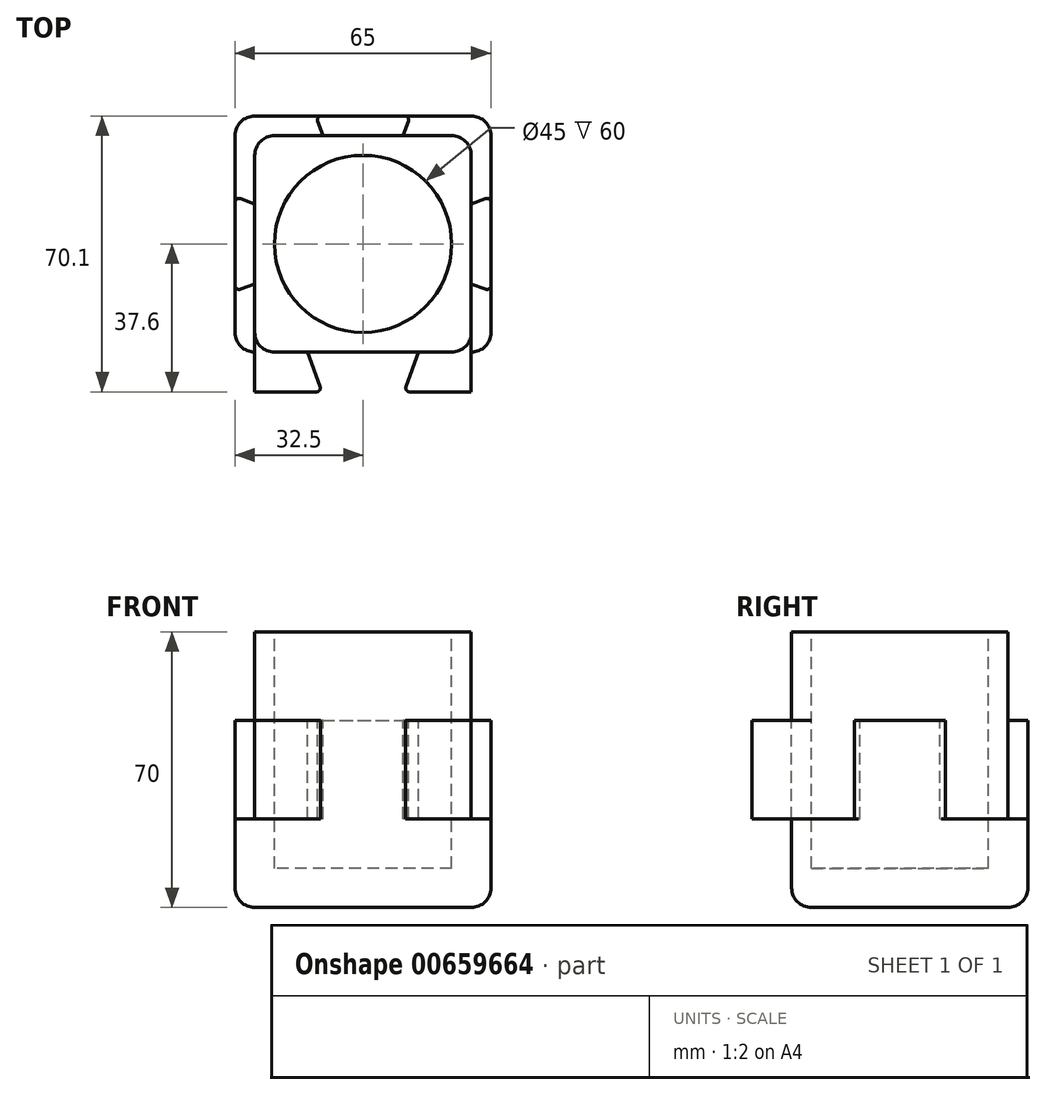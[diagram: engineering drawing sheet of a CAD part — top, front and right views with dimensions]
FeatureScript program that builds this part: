
annotation { "Feature Type Name" : "Feature", "Feature Type Description" : "" }
export const myFeature = defineFeature(function(context is Context, id is Id, definition is map)
    precondition{}
    {
        {
            var Q0;
            Q0=qCreatedBy(makeId("Top.planeOp"),FACE);
            var sketch = newSketch(context, id + "F0", { "sketchPlane" : qUnion([Q0])});
            skLineSegment(sketch, "E0.bottom", {"start": v(-27.5, 27.5) * mm, "end": v(27.5, 27.5) * mm});
            skLineSegment(sketch, "E0.top", {"start": v(-27.5, -27.5) * mm, "end": v(27.5, -27.5) * mm});
            skLineSegment(sketch, "E0.left", {"start": v(-27.5, 27.5) * mm, "end": v(-27.5, -27.5) * mm});
            skLineSegment(sketch, "E0.right", {"start": v(27.5, 27.5) * mm, "end": v(27.5, -27.5) * mm});
            skPoint(sketch, "E0.middle", {"position": v(0, 0) * mm});
            skLineSegment(sketch, "E1", {"start": v(27.5, -10.18) * mm, "end": v(32.5, -12) * mm});
            skLineSegment(sketch, "E2", {"start": v(32.5, -12) * mm, "end": v(32.5, 12) * mm});
            skLineSegment(sketch, "E3", {"start": v(32.5, 12) * mm, "end": v(27.5, 10.18) * mm});
            skPoint(sketch, "E4", {"position": v(32.5, 0) * mm});
            skLineSegment(sketch, "E5", {"start": v(-10.18, 27.5) * mm, "end": v(-12, 32.5) * mm});
            skLineSegment(sketch, "E6", {"start": v(-12, 32.5) * mm, "end": v(12, 32.5) * mm});
            skLineSegment(sketch, "E7", {"start": v(12, 32.5) * mm, "end": v(10.18, 27.5) * mm});
            skPoint(sketch, "E8", {"position": v(0, 32.5) * mm});
            skLineSegment(sketch, "E9", {"start": v(-27.5, 10.18) * mm, "end": v(-32.5, 12) * mm});
            skLineSegment(sketch, "E10", {"start": v(-32.5, 12) * mm, "end": v(-32.5, -12) * mm});
            skLineSegment(sketch, "E11", {"start": v(-32.5, -12) * mm, "end": v(-27.5, -10.18) * mm});
            skPoint(sketch, "E12", {"position": v(-32.5, 0) * mm});
            skLineSegment(sketch, "E13", {"start": v(-27.5, -27.5) * mm, "end": v(-27.5, -37.6) * mm});
            skLineSegment(sketch, "E14", {"start": v(-27.5, -37.6) * mm, "end": v(-10.42, -37.6) * mm});
            skLineSegment(sketch, "E15", {"start": v(-10.42, -37.6) * mm, "end": v(-14.1, -27.5) * mm});
            skLineSegment(sketch, "E16", {"start": v(27.5, -27.5) * mm, "end": v(27.5, -37.6) * mm});
            skLineSegment(sketch, "E17", {"start": v(27.5, -37.6) * mm, "end": v(10.42, -37.6) * mm});
            skLineSegment(sketch, "E18", {"start": v(10.42, -37.6) * mm, "end": v(14.1, -27.5) * mm});
            skSolve(sketch);
        }
        {
            var Q0;
            {var subQ1=sQuery(id+"F0.wireOp",EDGE,"E0.bottom");Q0=makeQuery(id+"F0.imprint","IMPRINT",FACE,{"disambiguationData":[TD([[makeQuery(id+"F0.imprint","IMPRINT",EDGE,{"derivedFrom":subQ1}),-1.0]])]});}
            extrude(context, id + "F1", {"entities" : qUnion([Q0]), "oppositeDirection" : true, "depth" : 70 * mm, "offsetDistance" : 25 * mm, "symmetric" : true});
        }
        {
            var Q0;
            {var subQ0=sQuery(id+"F0.wireOp",EDGE,"E5");Q0=makeQuery(id+"F0.imprint","IMPRINT",FACE,{"disambiguationData":[TD([[makeQuery(id+"F0.imprint","IMPRINT",EDGE,{"derivedFrom":subQ0}),-1.0]])]});}
            var Q1;
            {var subQ0=sQuery(id+"F0.wireOp",EDGE,"E9");Q1=makeQuery(id+"F0.imprint","IMPRINT",FACE,{"disambiguationData":[TD([[makeQuery(id+"F0.imprint","IMPRINT",EDGE,{"derivedFrom":subQ0}),1.0]])]});}
            var Q2;
            {var subQ2=sQuery(id+"F0.wireOp",EDGE,"E13");Q2=makeQuery(id+"F0.imprint","IMPRINT",FACE,{"disambiguationData":[TD([[makeQuery(id+"F0.imprint","IMPRINT",EDGE,{"derivedFrom":subQ2}),1.0]])]});}
            var Q3;
            {var subQ0=sQuery(id+"F0.wireOp",EDGE,"E16");Q3=makeQuery(id+"F0.imprint","IMPRINT",FACE,{"disambiguationData":[TD([[makeQuery(id+"F0.imprint","IMPRINT",EDGE,{"derivedFrom":subQ0}),-1.0]])]});}
            var Q4;
            {var subQ2=sQuery(id+"F0.wireOp",EDGE,"E1");Q4=makeQuery(id+"F0.imprint","IMPRINT",FACE,{"disambiguationData":[TD([[makeQuery(id+"F0.imprint","IMPRINT",EDGE,{"derivedFrom":subQ2}),1.0]])]});}
            extrude(context, id + "F2", {"entities" : qUnion([Q0, Q1, Q2, Q3, Q4]), "operationType" : NewBodyOperationType.ADD, "oppositeDirection" : true, "depth" : 25 * mm, "offsetDistance" : 25 * mm, "symmetric" : true});
        }
        {
            var Q0;
            Q0=makeQuery(id+"F1.opExtrude","CAP_FACE",FACE,{"disambiguationData":[OSD([sQuery(id+"F0.wireOp",EDGE,"E0.bottom"),sQuery(id+"F0.wireOp",EDGE,"E0.top"),sQuery(id+"F0.wireOp",EDGE,"E0.left"),sQuery(id+"F0.wireOp",EDGE,"E0.right")])],"isStart":false});
            var sketch = newSketch(context, id + "F3", { "sketchPlane" : qUnion([Q0])});
            skLineSegment(sketch, "E19", {"start": v(27.5, -27.5) * mm, "end": v(27.5, 27.5) * mm});
            skLineSegment(sketch, "E20", {"start": v(27.5, 27.5) * mm, "end": v(-27.5, 27.5) * mm});
            skLineSegment(sketch, "E21", {"start": v(27.5, -27.5) * mm, "end": v(-27.5, -27.5) * mm});
            skLineSegment(sketch, "E22", {"start": v(-27.5, -27.5) * mm, "end": v(-27.5, 27.5) * mm});
            skLineSegment(sketch, "E23", {"start": v(-32.5, 27.5) * mm, "end": v(32.5, 27.5) * mm});
            skLineSegment(sketch, "E24", {"start": v(32.5, 27.5) * mm, "end": v(32.5, -32.5) * mm});
            skLineSegment(sketch, "E25", {"start": v(32.5, -32.5) * mm, "end": v(-32.5, -32.5) * mm});
            skLineSegment(sketch, "E26", {"start": v(-32.5, -32.5) * mm, "end": v(-32.5, 27.5) * mm});
            skSolve(sketch);
        }
        {
            var Q0;
            Q0 = qSketchRegion(id + "F3", true);
            var Q1;
            Q1=makeQuery(id+"F2.opExtrude","CAP_FACE",FACE,{"disambiguationData":[OSD([sQuery(id+"F0.wireOp",EDGE,"E0.left"),sQuery(id+"F0.wireOp",EDGE,"E9"),sQuery(id+"F0.wireOp",EDGE,"E10"),sQuery(id+"F0.wireOp",EDGE,"E11")])],"isStart":false});
            extrude(context, id + "F4", {"entities" : qUnion([Q0]), "operationType" : NewBodyOperationType.ADD, "endBound" : BoundingType.UP_TO_SURFACE, "oppositeDirection" : true, "depth" : 25 * mm, "endBoundEntityFace" : qUnion([Q1]), "offsetDistance" : 25 * mm});
        }
        {
            var Q0;
            Q0=makeQuery(id+"F1.opExtrude","CAP_FACE",FACE,{"disambiguationData":[OSD([sQuery(id+"F0.wireOp",EDGE,"E0.bottom"),sQuery(id+"F0.wireOp",EDGE,"E0.top"),sQuery(id+"F0.wireOp",EDGE,"E0.left"),sQuery(id+"F0.wireOp",EDGE,"E0.right")])],"isStart":true});
            var sketch = newSketch(context, id + "F5", { "sketchPlane" : qUnion([Q0])});
            skCircle(sketch, "E27", {"center": v(0, 0) * mm, "radius": 22.5 * mm});
            skSolve(sketch);
        }
        {
            var Q0;
            Q0 = qSketchRegion(id + "F5", true);
            extrude(context, id + "F6", {"entities" : qUnion([Q0]), "operationType" : NewBodyOperationType.REMOVE, "oppositeDirection" : true, "depth" : 60 * mm, "offsetDistance" : 25 * mm});
        }
        {
            var Q0;
            {var subQ0=sQuery(id+"F0.wireOp",EDGE,"E13");var subQ1=sQuery(id+"F0.wireOp",EDGE,"E0.top");var subQ2=sQuery(id+"F0.wireOp",EDGE,"E0.left");Q0=makeQuery(id+"F2.boolean.opBoolean","SPLIT",EDGE,{"disambiguationData":[TD([makeQuery(id+"F1.opExtrude","CAP_FACE",FACE,{"disambiguationData":[OSD([sQuery(id+"F0.wireOp",EDGE,"E0.bottom"),subQ1,subQ2,sQuery(id+"F0.wireOp",EDGE,"E0.right")])],"isStart":true})])],"derivedFrom":makeQuery(id+"F1.opExtrude","SWEPT_EDGE",EDGE,{"disambiguationData":[OSD([subQ1,subQ2,subQ0])]})});}
            var Q1;
            Q1=makeQuery(id+"F4.opExtrude","SWEPT_EDGE",EDGE,{"disambiguationData":[OSD([sQuery(id+"F3.wireOp",EDGE,"E23"),sQuery(id+"F3.wireOp",EDGE,"E26")])]});
            var Q2;
            {var subQ0=sQuery(id+"F0.wireOp",EDGE,"E0.right");var subQ1=sQuery(id+"F0.wireOp",EDGE,"E16");var subQ2=sQuery(id+"F0.wireOp",EDGE,"E0.top");Q2=makeQuery(id+"F2.boolean.opBoolean","SPLIT",EDGE,{"disambiguationData":[TD([makeQuery(id+"F1.opExtrude","CAP_FACE",FACE,{"disambiguationData":[OSD([sQuery(id+"F0.wireOp",EDGE,"E0.bottom"),subQ2,sQuery(id+"F0.wireOp",EDGE,"E0.left"),subQ0])],"isStart":true})])],"derivedFrom":makeQuery(id+"F1.opExtrude","SWEPT_EDGE",EDGE,{"disambiguationData":[OSD([subQ2,subQ0,subQ1])]})});}
            var Q3;
            Q3=makeQuery(id+"F4.opExtrude","SWEPT_EDGE",EDGE,{"disambiguationData":[OSD([sQuery(id+"F3.wireOp",EDGE,"E23"),sQuery(id+"F3.wireOp",EDGE,"E24")])]});
            var Q4;
            Q4=makeQuery(id+"F1.opExtrude","SWEPT_EDGE",EDGE,{"disambiguationData":[OSD([sQuery(id+"F0.wireOp",EDGE,"E0.bottom"),sQuery(id+"F0.wireOp",EDGE,"E0.right")])]});
            var Q5;
            Q5=makeQuery(id+"F4.opExtrude","SWEPT_EDGE",EDGE,{"disambiguationData":[OSD([sQuery(id+"F3.wireOp",EDGE,"E24"),sQuery(id+"F3.wireOp",EDGE,"E25")])]});
            var Q6;
            Q6=makeQuery(id+"F1.opExtrude","SWEPT_EDGE",EDGE,{"disambiguationData":[OSD([sQuery(id+"F0.wireOp",EDGE,"E0.bottom"),sQuery(id+"F0.wireOp",EDGE,"E0.left")])]});
            var Q7;
            Q7=makeQuery(id+"F4.opExtrude","SWEPT_EDGE",EDGE,{"disambiguationData":[OSD([sQuery(id+"F3.wireOp",EDGE,"E25"),sQuery(id+"F3.wireOp",EDGE,"E26")])]});
            var Q8;
            Q8=makeQuery(id+"F4.boolean.opBoolean","MERGE",EDGE,{"derivedFrom":[makeQuery(id+"F1.opExtrude","CAP_EDGE",EDGE,{"disambiguationData":[OSD([sQuery(id+"F0.wireOp",EDGE,"E0.top")])],"isStart":false}),makeQuery(id+"F4.opExtrude","CAP_EDGE",EDGE,{"disambiguationData":[OSD([sQuery(id+"F3.wireOp",EDGE,"E20"),sQuery(id+"F3.wireOp",EDGE,"E23")])],"isStart":true})]});
            var Q9;
            Q9=makeQuery(id+"F4.opExtrude","CAP_EDGE",EDGE,{"disambiguationData":[OSD([sQuery(id+"F3.wireOp",EDGE,"E25")])],"isStart":true});
            var Q10;
            Q10=makeQuery(id+"F4.opExtrude","CAP_EDGE",EDGE,{"disambiguationData":[OSD([sQuery(id+"F3.wireOp",EDGE,"E24")])],"isStart":true});
            var Q11;
            Q11=makeQuery(id+"F4.opExtrude","CAP_EDGE",EDGE,{"disambiguationData":[OSD([sQuery(id+"F3.wireOp",EDGE,"E26")])],"isStart":true});
            fillet(context, id + "F7", {"entities" : qUnion([Q0, Q1, Q2, Q3, Q4, Q5, Q6, Q7, Q8, Q9, Q10, Q11]), "tangentPropagation" : true, "radius" : 5 * mm, "defaultsChanged" : false, "vertexSettings" : [], "allowEdgeOverflow" : false});
        }
        {
            var Q0;
            Q0=makeQuery(id+"F2.opExtrude","SWEPT_EDGE",EDGE,{"disambiguationData":[OSD([sQuery(id+"F0.wireOp",EDGE,"E2"),sQuery(id+"F0.wireOp",EDGE,"E3")])]});
            var Q1;
            Q1=makeQuery(id+"F2.opExtrude","SWEPT_EDGE",EDGE,{"disambiguationData":[OSD([sQuery(id+"F0.wireOp",EDGE,"E1"),sQuery(id+"F0.wireOp",EDGE,"E2")])]});
            var Q2;
            Q2=makeQuery(id+"F2.opExtrude","SWEPT_EDGE",EDGE,{"disambiguationData":[OSD([sQuery(id+"F0.wireOp",EDGE,"E17"),sQuery(id+"F0.wireOp",EDGE,"E18")])]});
            var Q3;
            Q3=makeQuery(id+"F2.opExtrude","SWEPT_EDGE",EDGE,{"disambiguationData":[OSD([sQuery(id+"F0.wireOp",EDGE,"E14"),sQuery(id+"F0.wireOp",EDGE,"E15")])]});
            var Q4;
            Q4=makeQuery(id+"F2.opExtrude","SWEPT_EDGE",EDGE,{"disambiguationData":[OSD([sQuery(id+"F0.wireOp",EDGE,"E10"),sQuery(id+"F0.wireOp",EDGE,"E11")])]});
            var Q5;
            Q5=makeQuery(id+"F2.opExtrude","SWEPT_EDGE",EDGE,{"disambiguationData":[OSD([sQuery(id+"F0.wireOp",EDGE,"E9"),sQuery(id+"F0.wireOp",EDGE,"E10")])]});
            var Q6;
            Q6=makeQuery(id+"F2.opExtrude","SWEPT_EDGE",EDGE,{"disambiguationData":[OSD([sQuery(id+"F0.wireOp",EDGE,"E5"),sQuery(id+"F0.wireOp",EDGE,"E6")])]});
            var Q7;
            Q7=makeQuery(id+"F2.opExtrude","SWEPT_EDGE",EDGE,{"disambiguationData":[OSD([sQuery(id+"F0.wireOp",EDGE,"E6"),sQuery(id+"F0.wireOp",EDGE,"E7")])]});
            fillet(context, id + "F8", {"entities" : qUnion([Q0, Q1, Q2, Q3, Q4, Q5, Q6, Q7]), "tangentPropagation" : true, "radius" : 1 * mm, "defaultsChanged" : false, "vertexSettings" : [], "allowEdgeOverflow" : false});
        }
        {
            var Q0;
            Q0=qCreatedBy(makeId("Top.planeOp"),FACE);
            cPlane(context, id + "F9", {"entities" : qUnion([Q0]), "cplaneType" : CPlaneType.OFFSET, "offset" : 10 * mm, "oppositeDirection" : true, "width" : 150 * mm, "height" : 150 * mm});
        }
    });
